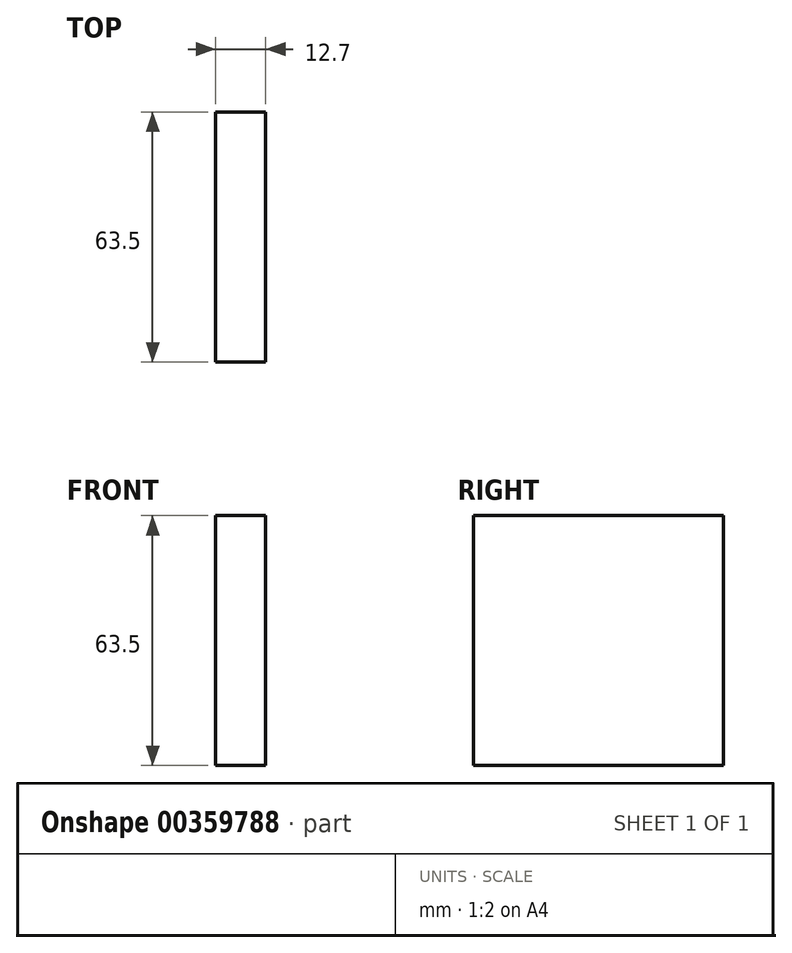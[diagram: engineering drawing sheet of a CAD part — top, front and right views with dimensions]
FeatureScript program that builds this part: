
annotation { "Feature Type Name" : "Feature", "Feature Type Description" : "" }
export const myFeature = defineFeature(function(context is Context, id is Id, definition is map)
    precondition{}
    {
        {
            var Q0;
            Q0=qCreatedBy(makeId("Front.planeOp"),FACE);
            var sketch = newSketch(context, id + "F0", { "sketchPlane" : qUnion([Q0])});
            skLineSegment(sketch, "E0.bottom", {"start": v(0, 0) * mm, "end": v(12.7, 0) * mm});
            skLineSegment(sketch, "E0.top", {"start": v(0, -63.5) * mm, "end": v(12.7, -63.5) * mm});
            skLineSegment(sketch, "E0.left", {"start": v(0, 0) * mm, "end": v(0, -63.5) * mm});
            skLineSegment(sketch, "E0.right", {"start": v(12.7, 0) * mm, "end": v(12.7, -63.5) * mm});
            skSolve(sketch);
        }
        {
            var Q0;
            Q0=makeQuery(id+"F0.imprint","IMPRINT",FACE,{"disambiguationData":[TD([[makeQuery(id+"F0.imprint","IMPRINT",EDGE,{"derivedFrom":sQuery(id+"F0.wireOp",EDGE,"E0.bottom")}),-1.0]])]});
            var Q1;
            Q1 = qSketchRegion(id + "F0", true);
            extrude(context, id + "F1", {"entities" : qUnion([Q0, Q1]), "depth" : 63.5 * mm});
        }
    });
